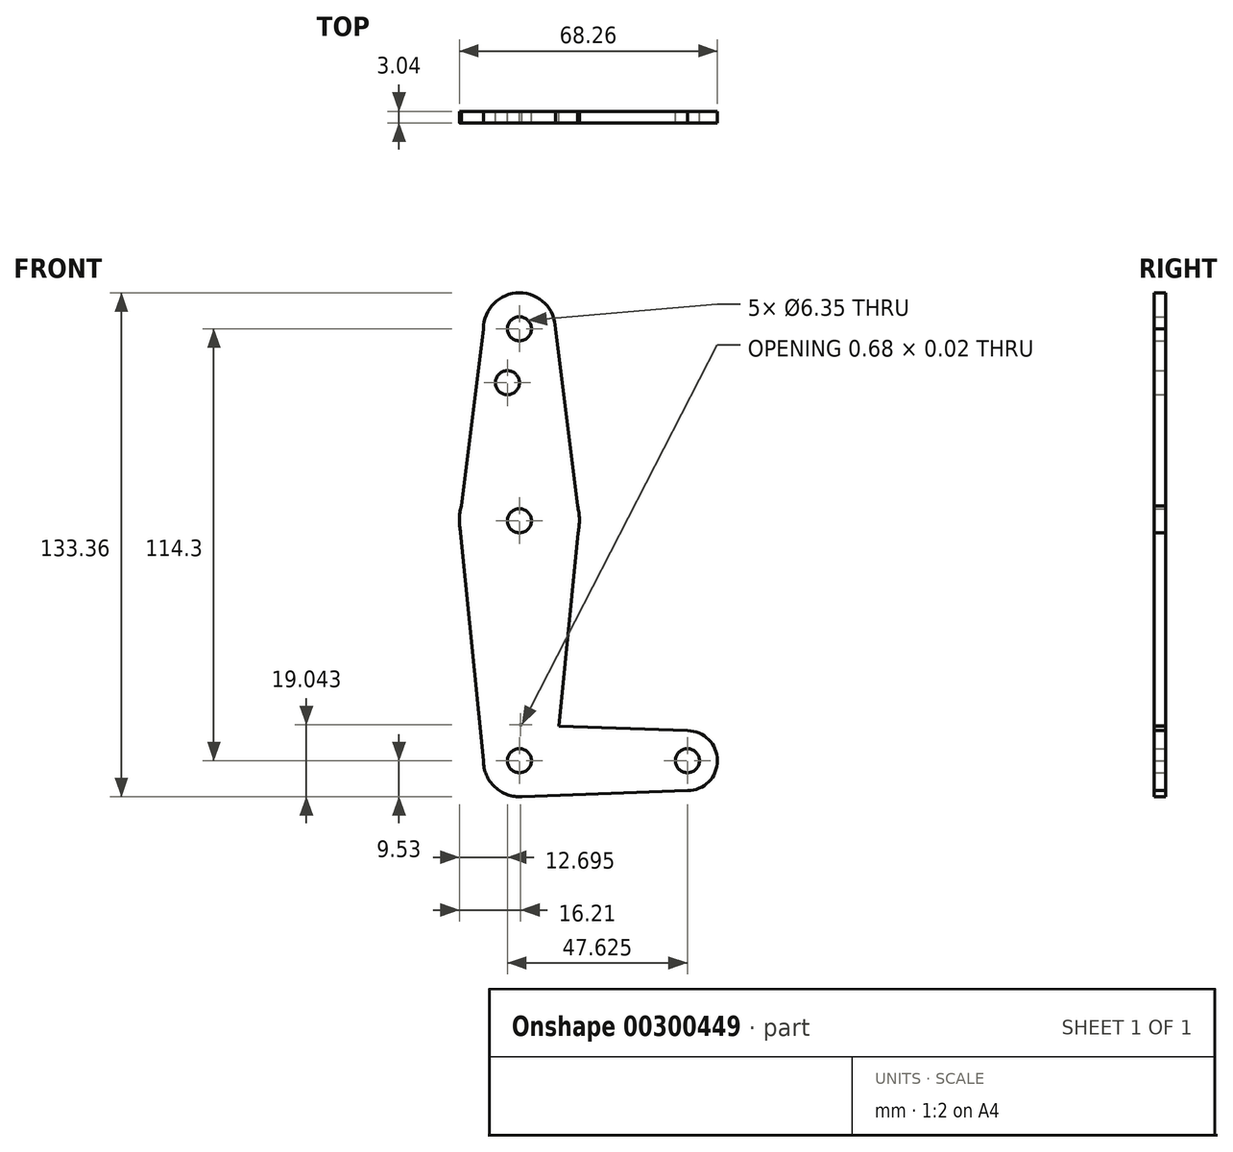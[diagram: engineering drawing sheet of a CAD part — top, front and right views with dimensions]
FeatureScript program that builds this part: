
annotation { "Feature Type Name" : "Feature", "Feature Type Description" : "" }
export const myFeature = defineFeature(function(context is Context, id is Id, definition is map)
    precondition{}
    {
        {
            var Q0;
            Q0=qCreatedBy(makeId("Front.planeOp"),FACE);
            var sketch = newSketch(context, id + "F0", { "sketchPlane" : qUnion([Q0])});
            skCircle(sketch, "E0", {"center": v(44.45, 0) * mm, "radius": 7.94 * mm});
            skCircle(sketch, "E1", {"center": v(0, 63.5) * mm, "radius": 15.88 * mm});
            skCircle(sketch, "E2", {"center": v(0, 114.3) * mm, "radius": 9.53 * mm});
            skCircle(sketch, "E3", {"center": v(0, 0) * mm, "radius": 9.53 * mm});
            skLineSegment(sketch, "E4", {"start": v(0, 63.5) * mm, "end": v(0, 114.3) * mm, "construction": true});
            skLineSegment(sketch, "E5", {"start": v(0, 63.5) * mm, "end": v(0, 0) * mm, "construction": true});
            skLineSegment(sketch, "E6", {"start": v(0, 0) * mm, "end": v(44.45, 0) * mm, "construction": true});
            skPoint(sketch, "E7", {"position": v(0, 9.53) * mm});
            skPoint(sketch, "E8", {"position": v(9.53, 0) * mm});
            skPoint(sketch, "E9", {"position": v(-9.53, 0) * mm});
            skPoint(sketch, "E10", {"position": v(0, -9.53) * mm});
            skPoint(sketch, "E11", {"position": v(44.45, -7.94) * mm});
            skPoint(sketch, "E12", {"position": v(44.45, 7.94) * mm});
            skPoint(sketch, "E13", {"position": v(36.51, 0) * mm});
            skPoint(sketch, "E14", {"position": v(52.39, 0) * mm});
            skLineSegment(sketch, "E15", {"start": v(0, 9.52) * mm, "end": v(44.45, 7.94) * mm});
            skLineSegment(sketch, "E16", {"start": v(0, -9.52) * mm, "end": v(44.45, -7.94) * mm});
            skPoint(sketch, "E17", {"position": v(0, 47.62) * mm});
            skPoint(sketch, "E18", {"position": v(0, 79.38) * mm});
            skPoint(sketch, "E19", {"position": v(15.87, 63.5) * mm});
            skPoint(sketch, "E20", {"position": v(-15.88, 63.5) * mm});
            skLineSegment(sketch, "E21", {"start": v(15.87, 63.5) * mm, "end": v(9.53, 0) * mm});
            skLineSegment(sketch, "E22", {"start": v(-15.88, 63.5) * mm, "end": v(-9.53, 0) * mm});
            skPoint(sketch, "E23", {"position": v(0, 104.78) * mm});
            skPoint(sketch, "E24", {"position": v(9.52, 114.3) * mm});
            skPoint(sketch, "E25", {"position": v(-9.53, 114.3) * mm});
            skLineSegment(sketch, "E26", {"start": v(-15.88, 63.5) * mm, "end": v(-9.53, 114.3) * mm});
            skLineSegment(sketch, "E27", {"start": v(9.52, 114.3) * mm, "end": v(15.87, 63.5) * mm});
            skCircle(sketch, "E28", {"center": v(0, 114.3) * mm, "radius": 3.18 * mm});
            skCircle(sketch, "E29", {"center": v(0, 63.5) * mm, "radius": 3.18 * mm});
            skCircle(sketch, "E30", {"center": v(44.45, 0) * mm, "radius": 3.18 * mm});
            skCircle(sketch, "E31", {"center": v(0, 0) * mm, "radius": 3.18 * mm});
            skCircle(sketch, "E32", {"center": v(-3.17, 100.03) * mm, "radius": 3.18 * mm});
            skSolve(sketch);
        }
        {
            var Q0;
            Q0 = qSketchRegion(id + "F0", true);
            extrude(context, id + "F1", {"entities" : qUnion([Q0]), "endBound" : BoundingType.SYMMETRIC, "depth" : 3.05 * mm});
        }
    });
